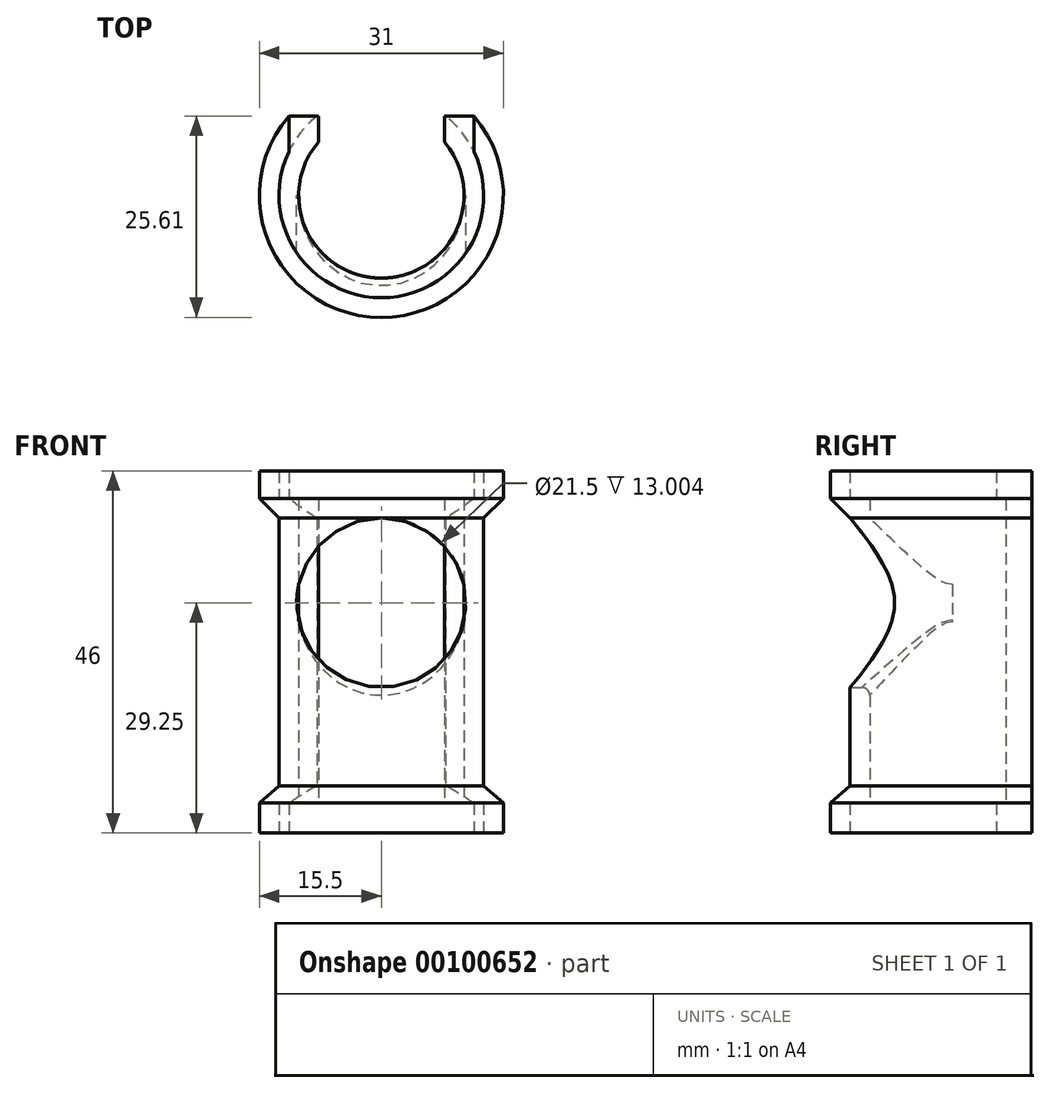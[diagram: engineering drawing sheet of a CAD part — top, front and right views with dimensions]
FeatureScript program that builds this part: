
annotation { "Feature Type Name" : "Feature", "Feature Type Description" : "" }
export const myFeature = defineFeature(function(context is Context, id is Id, definition is map)
    precondition{}
    {
        {
            var Q0;
            Q0=qCreatedBy(makeId("Front.planeOp"),FACE);
            var sketch = newSketch(context, id + "F0", { "sketchPlane" : qUnion([Q0])});
            skLineSegment(sketch, "E0", {"start": v(-13, 0) * mm, "end": v(-13, 3.8) * mm});
            skLineSegment(sketch, "E1", {"start": v(-13, 3.8) * mm, "end": v(-10.5, 3.8) * mm});
            skLineSegment(sketch, "E2", {"start": v(-10.5, 3.8) * mm, "end": v(-10.5, 42.5) * mm});
            skLineSegment(sketch, "E3", {"start": v(-13, 42.5) * mm, "end": v(-13, 46) * mm});
            skLineSegment(sketch, "E4", {"start": v(-13, 42.5) * mm, "end": v(-10.5, 42.5) * mm});
            skLineSegment(sketch, "E5", {"start": v(-13, 46) * mm, "end": v(-15.5, 46) * mm});
            skLineSegment(sketch, "E6", {"start": v(-15.5, 46) * mm, "end": v(-15.5, 42.5) * mm});
            skLineSegment(sketch, "E7", {"start": v(-13, 40) * mm, "end": v(-13, 6) * mm});
            skLineSegment(sketch, "E8", {"start": v(-15.5, 3.8) * mm, "end": v(-15.5, 0) * mm});
            skLineSegment(sketch, "E9", {"start": v(-15.5, 0) * mm, "end": v(-13, 0) * mm});
            skLineSegment(sketch, "E10", {"start": v(0, 0) * mm, "end": v(0, 49.8) * mm, "construction": true});
            skLineSegment(sketch, "E11", {"start": v(-15.5, 42.5) * mm, "end": v(-13, 40) * mm});
            skLineSegment(sketch, "E12", {"start": v(-15.5, 3.8) * mm, "end": v(-13, 6) * mm});
            skPoint(sketch, "E13.orphan", {"position": v(-13, 41) * mm});
            skPoint(sketch, "E14.orphan", {"position": v(-13, 3.5) * mm});
            skSolve(sketch);
        }
        {
            var Q0;
            Q0=qSketchRegion(id+"F0",true);
            var Q1;
            Q1=sQuery(id+"F0.wireOp",EDGE,"E10");
            revolve(context, id + "F1", {"entities" : qUnion([Q0]), "axis" : qUnion([Q1]), "revolveType" : RevolveType.FULL});
        }
        {
            var Q0;
            Q0=makeQuery(id+"F1.opRevolve","SWEPT_FACE",FACE,{"disambiguationData":[OSD([sQuery(id+"F0.wireOp",EDGE,"E5")])]});
            var sketch = newSketch(context, id + "F2", { "sketchPlane" : qUnion([Q0])});
            skLineSegment(sketch, "E15.bottom", {"start": v(-8, 18.1) * mm, "end": v(8, 18.1) * mm});
            skLineSegment(sketch, "E15.top", {"start": v(-8, 5.31) * mm, "end": v(8, 5.31) * mm});
            skLineSegment(sketch, "E15.left", {"start": v(-8, 18.1) * mm, "end": v(-8, 5.31) * mm});
            skLineSegment(sketch, "E15.right", {"start": v(8, 18.1) * mm, "end": v(8, 5.31) * mm});
            skSolve(sketch);
        }
        {
            var Q0;
            Q0=qSketchRegion(id+"F2",true);
            extrude(context, id + "F3", {"entities" : qUnion([Q0]), "operationType" : NewBodyOperationType.REMOVE, "endBound" : BoundingType.THROUGH_ALL, "oppositeDirection" : true, "depth" : 25 * mm});
        }
        {
            var Q0;
            Q0=makeQuery(id+"F1.opRevolve","SWEPT_FACE",FACE,{"disambiguationData":[OSD([sQuery(id+"F0.wireOp",EDGE,"E5")])]});
            var sketch = newSketch(context, id + "F4", { "sketchPlane" : qUnion([Q0])});
            skLineSegment(sketch, "E16.bottom", {"start": v(-11.75, 4.07) * mm, "end": v(11.75, 4.07) * mm});
            skLineSegment(sketch, "E16.top", {"start": v(-11.75, 17.53) * mm, "end": v(11.75, 17.53) * mm});
            skLineSegment(sketch, "E16.left", {"start": v(-11.75, 4.07) * mm, "end": v(-11.75, 17.53) * mm});
            skLineSegment(sketch, "E16.right", {"start": v(11.75, 4.07) * mm, "end": v(11.75, 17.53) * mm});
            skSolve(sketch);
        }
        {
            var Q0;
            Q0=qSketchRegion(id+"F4",true);
            var Q1;
            Q1=makeQuery(id+"F1.opRevolve","SWEPT_FACE",FACE,{"disambiguationData":[OSD([sQuery(id+"F0.wireOp",EDGE,"E4")])]});
            extrude(context, id + "F5", {"entities" : qUnion([Q0]), "operationType" : NewBodyOperationType.REMOVE, "endBound" : BoundingType.UP_TO_SURFACE, "oppositeDirection" : true, "endBoundEntityFace" : qUnion([Q1]), "depth" : 25 * mm});
        }
        {
            var Q0;
            Q0=makeQuery(id+"F1.opRevolve","SWEPT_FACE",FACE,{"disambiguationData":[OSD([sQuery(id+"F0.wireOp",EDGE,"E9")])]});
            var sketch = newSketch(context, id + "F6", { "sketchPlane" : qUnion([Q0])});
            skLineSegment(sketch, "E17.bottom", {"start": v(-11.75, -15.87) * mm, "end": v(11.75, -15.87) * mm});
            skLineSegment(sketch, "E17.top", {"start": v(-11.75, -2.84) * mm, "end": v(11.75, -2.84) * mm});
            skLineSegment(sketch, "E17.left", {"start": v(-11.75, -15.87) * mm, "end": v(-11.75, -2.84) * mm});
            skLineSegment(sketch, "E17.right", {"start": v(11.75, -15.87) * mm, "end": v(11.75, -2.84) * mm});
            skSolve(sketch);
        }
        {
            var Q0;
            Q0=qSketchRegion(id+"F6",true);
            var Q1;
            Q1=makeQuery(id+"F1.opRevolve","SWEPT_FACE",FACE,{"disambiguationData":[OSD([sQuery(id+"F0.wireOp",EDGE,"E1")])]});
            extrude(context, id + "F7", {"entities" : qUnion([Q0]), "operationType" : NewBodyOperationType.REMOVE, "endBound" : BoundingType.UP_TO_SURFACE, "oppositeDirection" : true, "endBoundEntityFace" : qUnion([Q1]), "depth" : 25 * mm});
        }
        {
            var Q0;
            Q0=qCreatedBy(makeId("Front.planeOp"),FACE);
            var sketch = newSketch(context, id + "F8", { "sketchPlane" : qUnion([Q0])});
            skCircle(sketch, "E18", {"center": v(0, 29.25) * mm, "radius": 10.75 * mm});
            skSolve(sketch);
        }
        {
            var Q0;
            Q0=makeQuery(id+"F8.imprint","IMPRINT",FACE,{"disambiguationData":[TD([[makeQuery(id+"F8.imprint","IMPRINT",EDGE,{"derivedFrom":sQuery(id+"F8.wireOp",EDGE,"E18")}),1.0]])]});
            extrude(context, id + "F9", {"entities" : qUnion([Q0]), "operationType" : NewBodyOperationType.REMOVE, "depth" : 25 * mm});
        }
        {
            var Q0;
            Q0=qCreatedBy(makeId("Right.planeOp"),FACE);
            var sketch = newSketch(context, id + "F10", { "sketchPlane" : qUnion([Q0])});
            skLineSegment(sketch, "E19.bottom", {"start": v(2, 37) * mm, "end": v(2, 37) * mm});
            skLineSegment(sketch, "E19.top", {"start": v(2, 12) * mm, "end": v(2, 12) * mm});
            skLineSegment(sketch, "E19.left", {"start": v(-1.5, 33.5) * mm, "end": v(-1.5, 15.5) * mm});
            skLineSegment(sketch, "E19.right", {"start": v(5.5, 33.5) * mm, "end": v(5.5, 15.5) * mm});
            skPoint(sketch, "E20.visualSharp", {"position": v(5.5, 37) * mm});
            skArc(sketch, "E20.filletArc", {"start": v(5.5, 33.5) * mm, "mid": v(4.47, 35.97) * mm, "end": v(2, 37) * mm});
            skPoint(sketch, "E21.visualSharp", {"position": v(5.5, 12) * mm});
            skArc(sketch, "E21.filletArc", {"start": v(2, 12) * mm, "mid": v(4.47, 13.03) * mm, "end": v(5.5, 15.5) * mm});
            skPoint(sketch, "E22.visualSharp", {"position": v(-1.5, 12) * mm});
            skArc(sketch, "E22.filletArc", {"start": v(-1.5, 15.5) * mm, "mid": v(-0.47, 13.03) * mm, "end": v(2, 12) * mm});
            skPoint(sketch, "E23.visualSharp", {"position": v(-1.5, 37) * mm});
            skArc(sketch, "E23.filletArc", {"start": v(2, 37) * mm, "mid": v(-0.47, 35.97) * mm, "end": v(-1.5, 33.5) * mm});
            skSolve(sketch);
        }
        {
            var Q0;
            Q0=qCreatedBy(makeId("Top.planeOp"),FACE);
            var sketch = newSketch(context, id + "F11", { "sketchPlane" : qUnion([Q0])});
            skLineSegment(sketch, "E24.bottom", {"start": v(-15.82, 20.1) * mm, "end": v(15.95, 20.1) * mm});
            skLineSegment(sketch, "E24.top", {"start": v(-15.82, 10.1) * mm, "end": v(15.95, 10.1) * mm});
            skLineSegment(sketch, "E24.left", {"start": v(-15.82, 20.1) * mm, "end": v(-15.82, 10.1) * mm});
            skLineSegment(sketch, "E24.right", {"start": v(15.95, 20.1) * mm, "end": v(15.95, 10.1) * mm});
            skSolve(sketch);
        }
        {
            var Q0;
            Q0=makeQuery(id+"F11.imprint","IMPRINT",FACE,{"disambiguationData":[TD([[makeQuery(id+"F11.imprint","IMPRINT",EDGE,{"derivedFrom":sQuery(id+"F11.wireOp",EDGE,"E24.bottom")}),-1.0]])]});
            extrude(context, id + "F12", {"entities" : qUnion([Q0]), "operationType" : NewBodyOperationType.REMOVE, "endBound" : BoundingType.THROUGH_ALL, "depth" : 25 * mm});
        }
        {
            var Q0;
            Q0=qCreatedBy(makeId("Front.planeOp"),FACE);
            var sketch = newSketch(context, id + "F13", { "sketchPlane" : qUnion([Q0])});
            skLineSegment(sketch, "E25.bottom", {"start": v(-0.5, 16.5) * mm, "end": v(0.5, 16.5) * mm});
            skLineSegment(sketch, "E25.top", {"start": v(-0.5, 8.5) * mm, "end": v(0.5, 8.5) * mm});
            skLineSegment(sketch, "E25.left", {"start": v(-4, 13) * mm, "end": v(-4, 12) * mm});
            skLineSegment(sketch, "E25.right", {"start": v(4, 13) * mm, "end": v(4, 12) * mm});
            skPoint(sketch, "E26.visualSharp", {"position": v(-4, 16.5) * mm});
            skArc(sketch, "E26.filletArc", {"start": v(-0.5, 16.5) * mm, "mid": v(-2.97, 15.47) * mm, "end": v(-4, 13) * mm});
            skPoint(sketch, "E27.visualSharp", {"position": v(4, 16.5) * mm});
            skArc(sketch, "E27.filletArc", {"start": v(4, 13) * mm, "mid": v(2.97, 15.47) * mm, "end": v(0.5, 16.5) * mm});
            skPoint(sketch, "E28.visualSharp", {"position": v(-4, 8.5) * mm});
            skArc(sketch, "E28.filletArc", {"start": v(-4, 12) * mm, "mid": v(-2.97, 9.53) * mm, "end": v(-0.5, 8.5) * mm});
            skPoint(sketch, "E29.visualSharp", {"position": v(4, 8.5) * mm});
            skArc(sketch, "E29.filletArc", {"start": v(0.5, 8.5) * mm, "mid": v(2.97, 9.53) * mm, "end": v(4, 12) * mm});
            skSolve(sketch);
        }
        {
            var Q0;
            Q0=makeQuery(id+"F9.boolean.opBoolean","INTERSECT",EDGE,{"disambiguationData":[OD(0.0)],"derivedFrom":[makeQuery(id+"F1.opRevolve","SWEPT_FACE",FACE,{"disambiguationData":[OSD([sQuery(id+"F0.wireOp",EDGE,"E2")])]}),makeQuery(id+"F9.opExtrude","SWEPT_FACE",FACE,{"disambiguationData":[OSD([sQuery(id+"F8.wireOp",EDGE,"E18")])]})]});
            fillet(context, id + "F14", {"entities" : qUnion([Q0]), "radius" : 1 * mm, "tangentPropagation" : true, "allowEdgeOverflow" : false});
        }
    });
